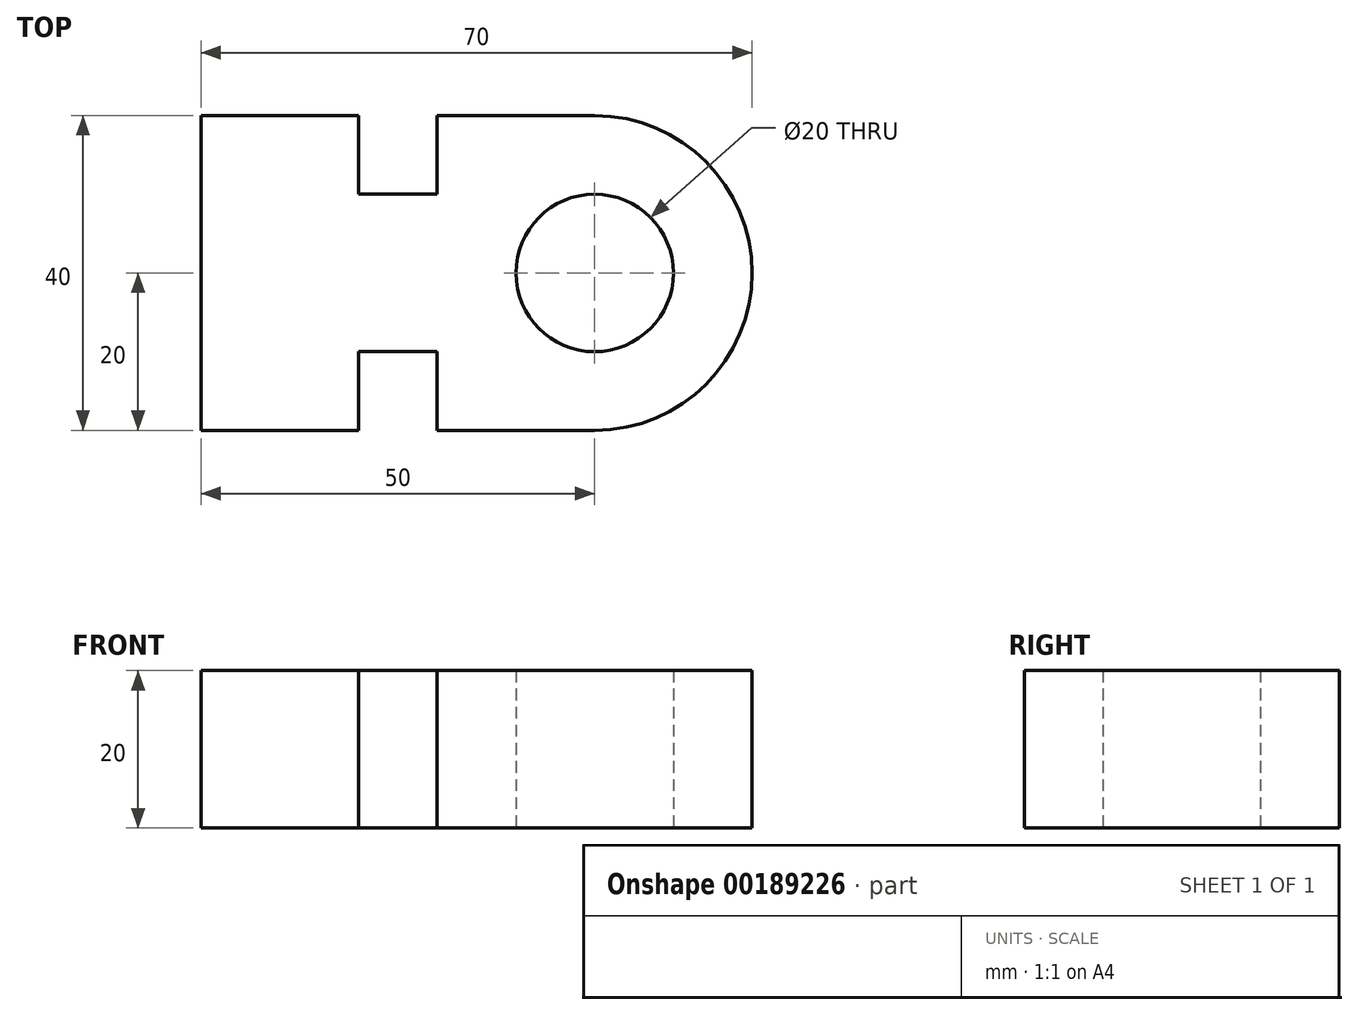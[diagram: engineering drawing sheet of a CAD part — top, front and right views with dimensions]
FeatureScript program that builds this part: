
annotation { "Feature Type Name" : "Feature", "Feature Type Description" : "" }
export const myFeature = defineFeature(function(context is Context, id is Id, definition is map)
    precondition{}
    {
        {
            var Q0;
            Q0=qCreatedBy(makeId("Top.planeOp"),FACE);
            var sketch = newSketch(context, id + "F0", { "sketchPlane" : qUnion([Q0])});
            skLineSegment(sketch, "E0", {"start": v(0, 0) * mm, "end": v(143.83, 0) * mm, "construction": true});
            skLineSegment(sketch, "E1", {"start": v(0, 0) * mm, "end": v(0, -20) * mm});
            skLineSegment(sketch, "E2", {"start": v(0, -20) * mm, "end": v(20, -20) * mm});
            skLineSegment(sketch, "E3", {"start": v(20, -20) * mm, "end": v(20, -10) * mm});
            skLineSegment(sketch, "E4", {"start": v(20, -10) * mm, "end": v(30, -10) * mm});
            skLineSegment(sketch, "E5", {"start": v(30, -10) * mm, "end": v(30, -20) * mm});
            skLineSegment(sketch, "E6", {"start": v(30, -20) * mm, "end": v(50, -20) * mm});
            skLineSegment(sketch, "E7", {"start": v(70, 0) * mm, "end": v(70, 0) * mm});
            skPoint(sketch, "E8.visualSharp", {"position": v(70, -20) * mm});
            skArc(sketch, "E8.filletArc", {"start": v(50, -20) * mm, "mid": v(64.14, -14.14) * mm, "end": v(70, 0) * mm});
            skLineSegment(sketch, "E9.MirrorCS", {"start": v(0, 0) * mm, "end": v(0, 20) * mm});
            skLineSegment(sketch, "E10.MirrorCS", {"start": v(0, 20) * mm, "end": v(20, 20) * mm});
            skLineSegment(sketch, "E11.MirrorCS", {"start": v(20, 20) * mm, "end": v(20, 10) * mm});
            skLineSegment(sketch, "E12.MirrorCS", {"start": v(20, 10) * mm, "end": v(30, 10) * mm});
            skLineSegment(sketch, "E13.MirrorCS", {"start": v(30, 20) * mm, "end": v(50, 20) * mm});
            skArc(sketch, "E14.MirrorCS", {"start": v(50, 20) * mm, "mid": v(64.14, 14.14) * mm, "end": v(70, 0) * mm});
            skLineSegment(sketch, "E15.MirrorCS", {"start": v(30, 10) * mm, "end": v(30, 20) * mm});
            skCircle(sketch, "E16", {"center": v(50, 0) * mm, "radius": 10 * mm});
            skSolve(sketch);
        }
        {
            var Q0;
            Q0=makeQuery(id+"F0.imprint","IMPRINT",FACE,{"disambiguationData":[TD([[makeQuery(id+"F0.imprint","IMPRINT",EDGE,{"derivedFrom":sQuery(id+"F0.wireOp",EDGE,"E1")}),1.0]])]});
            extrude(context, id + "F1", {"entities" : qUnion([Q0]), "depth" : 20 * mm});
        }
    });
